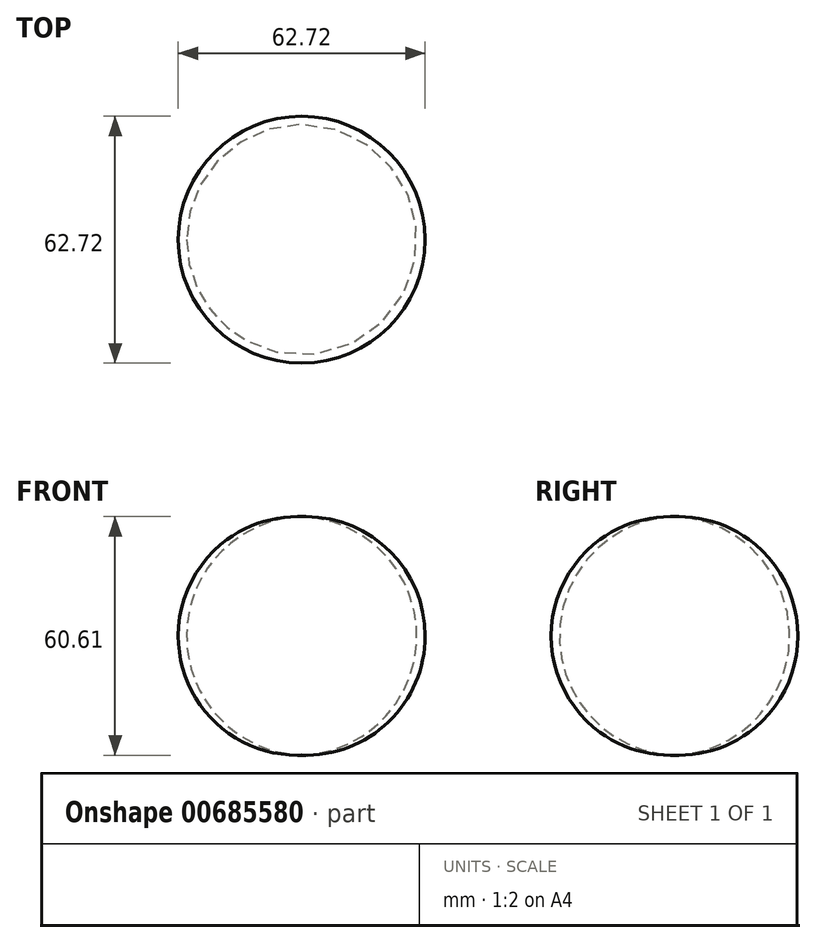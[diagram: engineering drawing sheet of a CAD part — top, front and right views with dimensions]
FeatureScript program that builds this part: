
annotation { "Feature Type Name" : "Feature", "Feature Type Description" : "" }
export const myFeature = defineFeature(function(context is Context, id is Id, definition is map)
    precondition{}
    {
        {
            var Q0;
            Q0=qCreatedBy(makeId("Front.planeOp"),FACE);
            var sketch = newSketch(context, id + "F0", { "sketchPlane" : qUnion([Q0])});
            skArc(sketch, "E0", {"start": v(0, 60.57) * mm, "mid": v(-29.25, 30.29) * mm, "end": v(0, 0) * mm});
            skLineSegment(sketch, "E1", {"start": v(0, 60.57) * mm, "end": v(0, 0) * mm});
            skSolve(sketch);
        }
        {
            var Q0;
            Q0=makeQuery(id+"F0.imprint","IMPRINT",FACE,{"disambiguationData":[TD([[makeQuery(id+"F0.imprint","IMPRINT",EDGE,{"derivedFrom":sQuery(id+"F0.wireOp",EDGE,"E0")}),1.0]])]});
            var Q1;
            Q1=sQuery(id+"F0.wireOp",EDGE,"E1");
            revolve(context, id + "F1", {"entities" : qUnion([Q0]), "axis" : qUnion([Q1]), "revolveType" : RevolveType.FULL});
        }
    });
